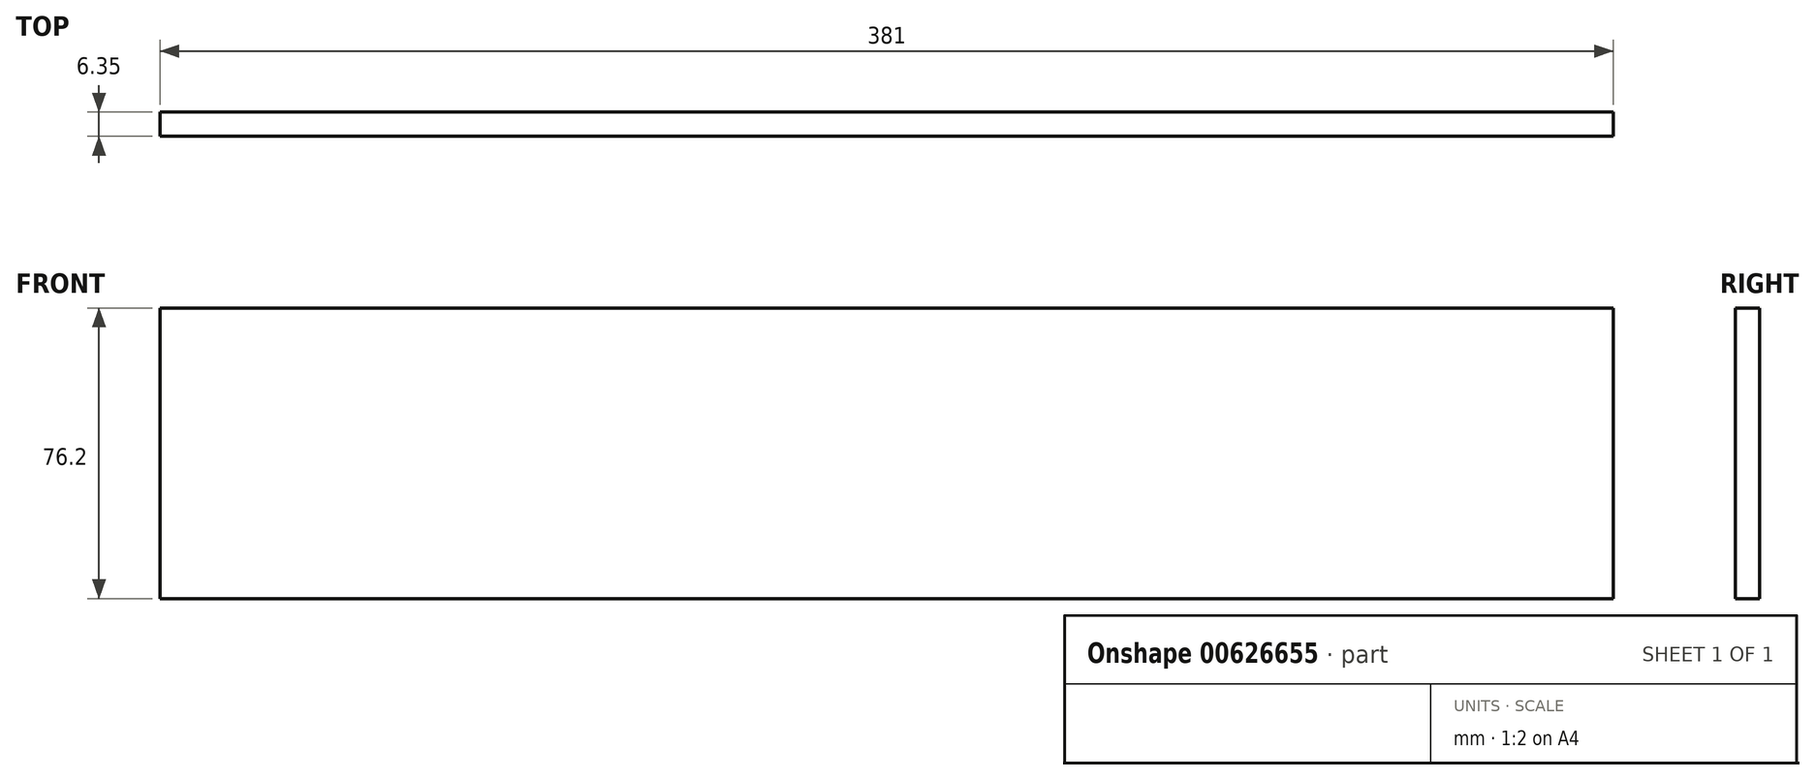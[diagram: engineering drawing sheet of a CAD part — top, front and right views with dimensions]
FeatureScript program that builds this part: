
annotation { "Feature Type Name" : "Feature", "Feature Type Description" : "" }
export const myFeature = defineFeature(function(context is Context, id is Id, definition is map)
    precondition{}
    {
        {
            var Q0;
            Q0=qCreatedBy(makeId("Front.planeOp"),FACE);
            var sketch = newSketch(context, id + "F0", { "sketchPlane" : qUnion([Q0])});
            skLineSegment(sketch, "E0.bottom", {"start": v(0, 0) * mm, "end": v(381, 0) * mm});
            skLineSegment(sketch, "E0.top", {"start": v(0, 76.2) * mm, "end": v(381, 76.2) * mm});
            skLineSegment(sketch, "E0.left", {"start": v(0, 0) * mm, "end": v(0, 76.2) * mm});
            skLineSegment(sketch, "E0.right", {"start": v(381, 0) * mm, "end": v(381, 76.2) * mm});
            skSolve(sketch);
        }
        {
            var Q0;
            Q0=makeQuery(id+"F0.imprint","IMPRINT",FACE,{"disambiguationData":[TD([[makeQuery(id+"F0.imprint","IMPRINT",EDGE,{"derivedFrom":sQuery(id+"F0.wireOp",EDGE,"E0.bottom")}),1.0]])]});
            extrude(context, id + "F1", {"entities" : qUnion([Q0]), "depth" : 6.35 * mm, "offsetDistance" : 25.4 * mm});
        }
    });
